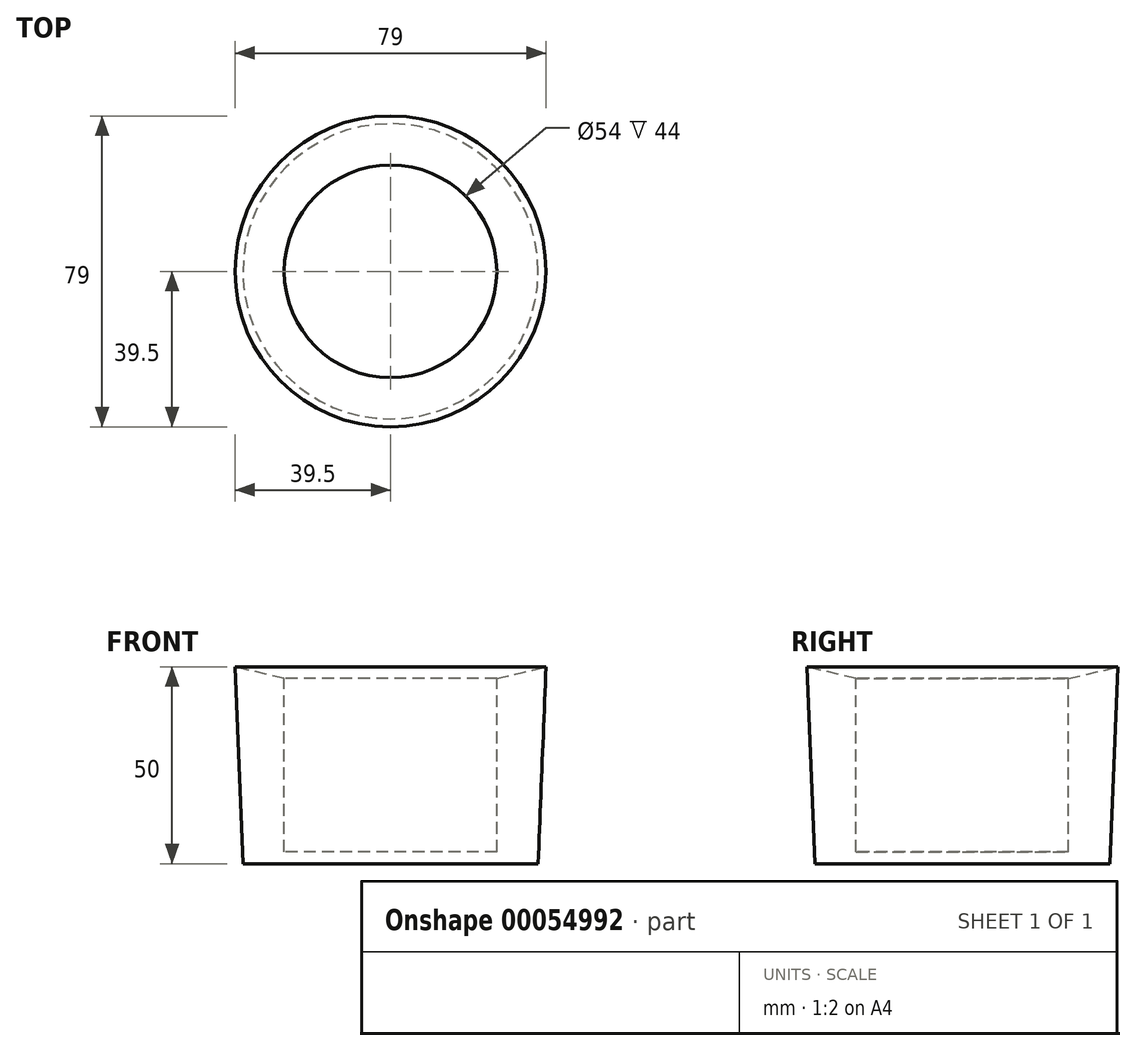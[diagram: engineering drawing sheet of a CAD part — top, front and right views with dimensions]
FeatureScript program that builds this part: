
annotation { "Feature Type Name" : "Feature", "Feature Type Description" : "" }
export const myFeature = defineFeature(function(context is Context, id is Id, definition is map)
    precondition{}
    {
        {
            var Q0;
            Q0=qCreatedBy(makeId("Right.planeOp"),FACE);
            var sketch = newSketch(context, id + "F0", { "sketchPlane" : qUnion([Q0])});
            skLineSegment(sketch, "E0", {"start": v(-39.5, 50) * mm, "end": v(-27, 47) * mm});
            skLineSegment(sketch, "E1", {"start": v(-27, 47) * mm, "end": v(-27, 3) * mm});
            skLineSegment(sketch, "E2", {"start": v(-27, 3) * mm, "end": v(0, 3) * mm});
            skLineSegment(sketch, "E3", {"start": v(0, 3) * mm, "end": v(0, 0) * mm});
            skLineSegment(sketch, "E4", {"start": v(0, 0) * mm, "end": v(-37.5, 0) * mm});
            skLineSegment(sketch, "E5", {"start": v(-37.5, 0) * mm, "end": v(-39.5, 50) * mm});
            skSolve(sketch);
        }
        {
            var Q0;
            Q0 = qSketchRegion(id + "F0", true);
            var Q1;
            Q1=sQuery(id+"F0.wireOp",EDGE,"E3");
            revolve(context, id + "F1", {"entities" : qUnion([Q0]), "axis" : qUnion([Q1]), "revolveType" : RevolveType.FULL});
        }
    });
